# Revit family: ledflood-e3_re246-100w-830-bl-as_709000116200
name_source: partatom
category: Lighting Fixtures
units: mm (PartAtom-declared; Revit-internal decimal feet)

## family parameters
Cut with Voids When Loaded = No
Host = Face
Light Source = No
Part Type = Normal
Room Calculation Point = No
Round Connector Dimension = Use Diameter
Shared = No

## types (1)
- LEDFlood-E3 Re246-100W-830-BL-AS (1 x LED, 14000 lm, 3000)
    Apparent Load = 100 VA
    CIE Flux Codes = 53 91 99 100 100
    Color Rendering = 80
    Color Temperature = 3000
    Control Gear = Electronic ballast
    Default Elevation = 1800 mm
    Description = Floodlight EcoMax G3 100W-14000lm-3000K
    Height = 40 mm  [stored 0.131234 ft]
    Lamp = 1 x LED
    Lamp Light Flux = 14000 lm
    Lamp count = 1
    Length = 286 mm
    Luminous efficacy = 140 lm/W
    Manufacturer = OPPLE
    ModVariant = No
    Model = 709000116200
    Mounting Place = Ceiling
    Mounting Type = Surface mounted
    Number of Poles = 1
    OnlyDefault = Yes
    Power Factor = 1
    Product Name = LEDFlood-E3 Re246-100W-830-BL-AS
    Product group = Filament A60
    ProductGroupID = 310
    Protection Class = Protection class I
    Protection Degree = IP 66
    RLX_Detail_Level = 1
    RLX_Emergency_Light_Flux = 0 lm
    RLX_Emergency_Type = 0
    RLX_Emergency_Type_DB = No
    RlxData = <blob elided: 254029 chars, md5=67fa1797>
    Socket = socket
    Standby Power = 0 W
    System Light Flux = 13999 lm
    System Power = 100 W
    Type Comments = Product without accessories
    Type Image = web_fl_eco_g3_as.jpg
    URL = http://relux.com
    VarID = ---
    Voltage = 0 V
    Weight = 0.00 kg
    Width = 236 mm

note: [stored X ft] marks values corroborated as IEEE doubles in the binary element streams (Revit-internal decimal feet)

## geometry (parser evidence)
native form markers: Blend x4, Sweep x13
no freeform markers — native parametric forms only
